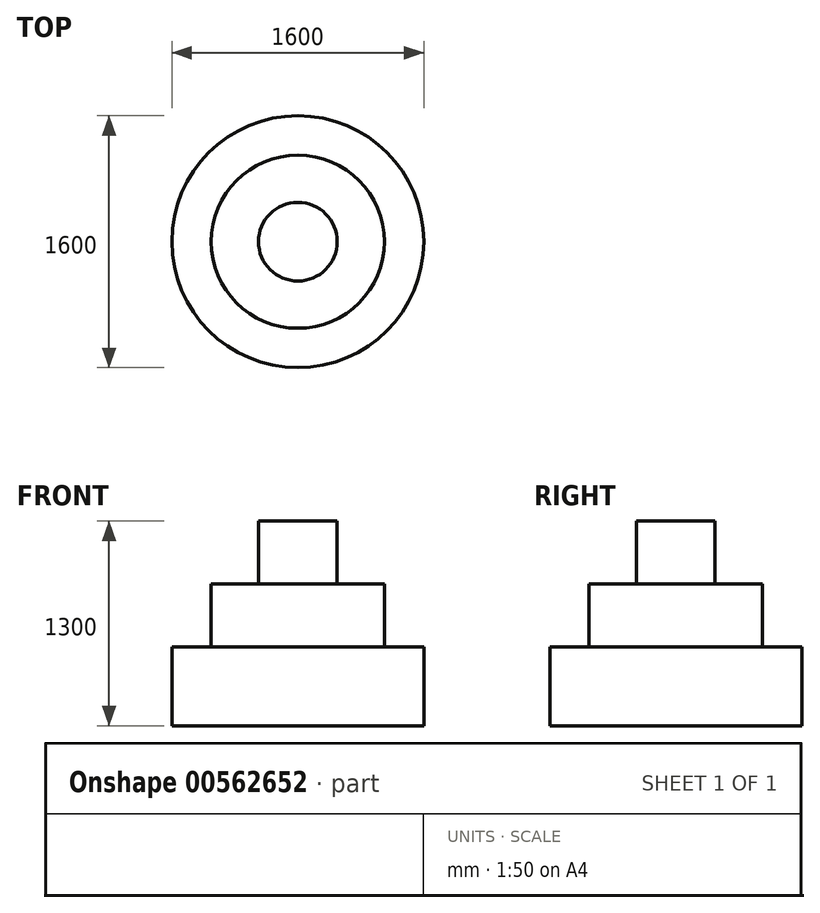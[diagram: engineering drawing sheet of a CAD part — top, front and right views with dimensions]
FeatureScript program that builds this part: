
annotation { "Feature Type Name" : "Feature", "Feature Type Description" : "" }
export const myFeature = defineFeature(function(context is Context, id is Id, definition is map)
    precondition{}
    {
        {
            var Q0;
            Q0=qCreatedBy(makeId("Top.planeOp"),FACE);
            var sketch = newSketch(context, id + "F0", { "sketchPlane" : qUnion([Q0])});
            skCircle(sketch, "E0", {"center": v(0, 0) * mm, "radius": 800 * mm});
            skSolve(sketch);
        }
        {
            var Q0;
            Q0=makeQuery(id+"F0.imprint","IMPRINT",FACE,{"disambiguationData":[TD([[makeQuery(id+"F0.imprint","IMPRINT",EDGE,{"derivedFrom":sQuery(id+"F0.wireOp",EDGE,"E0")}),1.0]])]});
            extrude(context, id + "F1", {"entities" : qUnion([Q0]), "depth" : 500 * mm, "offsetDistance" : 25 * mm});
        }
        {
            var Q0;
            Q0=makeQuery(id+"F1.opExtrude","CAP_FACE",FACE,{"disambiguationData":[OSD([sQuery(id+"F0.wireOp",EDGE,"E0")])],"isStart":false});
            var sketch = newSketch(context, id + "F2", { "sketchPlane" : qUnion([Q0])});
            skCircle(sketch, "E1", {"center": v(0, 0) * mm, "radius": 550 * mm});
            skSolve(sketch);
        }
        {
            var Q0;
            Q0=makeQuery(id+"F2.imprint","IMPRINT",FACE,{"disambiguationData":[TD([[makeQuery(id+"F2.imprint","IMPRINT",EDGE,{"derivedFrom":sQuery(id+"F2.wireOp",EDGE,"E1")}),1.0]])]});
            extrude(context, id + "F3", {"entities" : qUnion([Q0]), "depth" : 400 * mm, "offsetDistance" : 25 * mm});
        }
        {
            var Q0;
            Q0=makeQuery(id+"F3.opExtrude","CAP_FACE",FACE,{"disambiguationData":[OSD([sQuery(id+"F2.wireOp",EDGE,"E1")])],"isStart":false});
            var sketch = newSketch(context, id + "F4", { "sketchPlane" : qUnion([Q0])});
            skCircle(sketch, "E2", {"center": v(0, 0) * mm, "radius": 250 * mm});
            skSolve(sketch);
        }
        {
            var Q0;
            Q0 = qSketchRegion(id + "F4", true);
            extrude(context, id + "F5", {"entities" : qUnion([Q0]), "operationType" : NewBodyOperationType.ADD, "depth" : 400 * mm, "offsetDistance" : 25 * mm});
        }
    });
